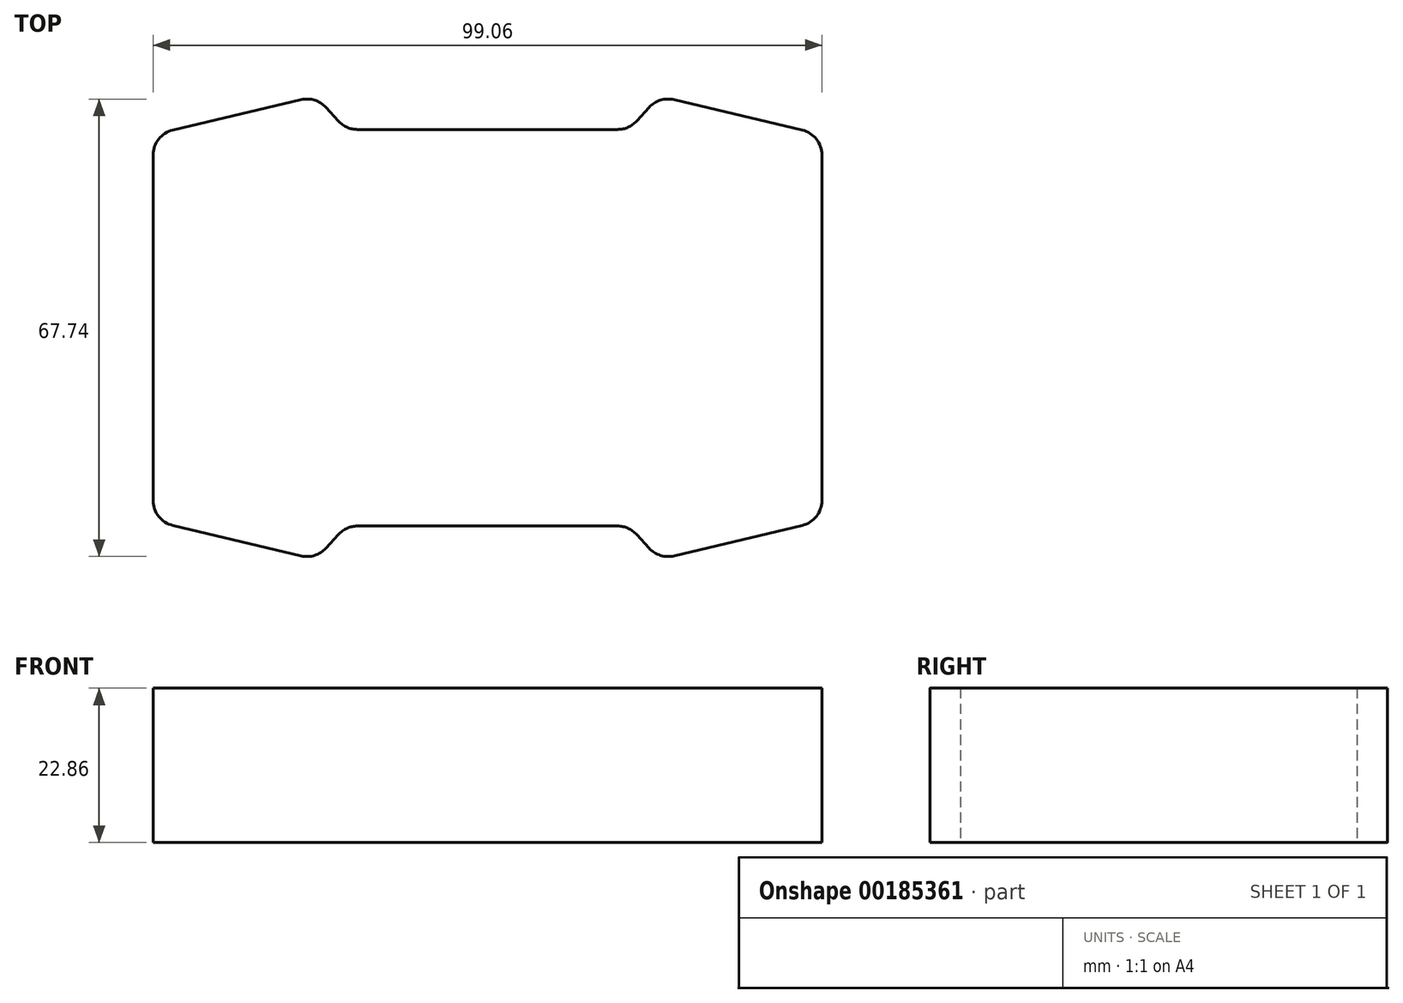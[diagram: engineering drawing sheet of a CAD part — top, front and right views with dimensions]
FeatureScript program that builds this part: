
annotation { "Feature Type Name" : "Feature", "Feature Type Description" : "" }
export const myFeature = defineFeature(function(context is Context, id is Id, definition is map)
    precondition{}
    {
        {
            var Q0;
            Q0=qCreatedBy(makeId("Top.planeOp"),FACE);
            var sketch = newSketch(context, id + "F0", { "sketchPlane" : qUnion([Q0])});
            skLineSegment(sketch, "E0.left", {"start": v(165.1, 95.25) * mm, "end": v(165.1, -95.25) * mm});
            skLineSegment(sketch, "E0.right", {"start": v(-165.1, 95.25) * mm, "end": v(-165.1, -95.25) * mm});
            skPoint(sketch, "E0.middle", {"position": v(0, 0) * mm});
            skLineSegment(sketch, "E1", {"start": v(-165.1, 95.25) * mm, "end": v(-84.78, 114.3) * mm});
            skLineSegment(sketch, "E2", {"start": v(-84.78, 114.3) * mm, "end": v(-69.85, 97.88) * mm});
            skLineSegment(sketch, "E3", {"start": v(-69.85, 97.88) * mm, "end": v(0, 97.88) * mm});
            skLineSegment(sketch, "E4.MirrorCS", {"start": v(165.1, 95.25) * mm, "end": v(84.78, 114.3) * mm});
            skLineSegment(sketch, "E5.MirrorCS", {"start": v(84.78, 114.3) * mm, "end": v(69.85, 97.88) * mm});
            skLineSegment(sketch, "E6.MirrorCS", {"start": v(69.85, 97.88) * mm, "end": v(0, 97.88) * mm});
            skLineSegment(sketch, "E7.MirrorCS", {"start": v(-165.1, -95.25) * mm, "end": v(-84.78, -114.3) * mm});
            skLineSegment(sketch, "E8.MirrorCS", {"start": v(-84.78, -114.3) * mm, "end": v(-69.85, -97.88) * mm});
            skLineSegment(sketch, "E9.MirrorCS", {"start": v(-69.85, -97.88) * mm, "end": v(0, -97.88) * mm});
            skLineSegment(sketch, "E10.MirrorCS", {"start": v(69.85, -97.88) * mm, "end": v(0, -97.88) * mm});
            skLineSegment(sketch, "E11.MirrorCS", {"start": v(84.78, -114.3) * mm, "end": v(69.85, -97.88) * mm});
            skLineSegment(sketch, "E12.MirrorCS", {"start": v(165.1, -95.25) * mm, "end": v(84.78, -114.3) * mm});
            skPoint(sketch, "E13.orphan", {"position": v(-165.1, 114.3) * mm});
            skPoint(sketch, "E14.orphan", {"position": v(165.1, 114.3) * mm});
            skPoint(sketch, "E15.orphan", {"position": v(165.1, -114.3) * mm});
            skPoint(sketch, "E16.orphan", {"position": v(-165.1, -114.3) * mm});
            skSolve(sketch);
        }
        {
            var Q0;
            Q0=qSketchRegion(id+"F0",true);
            extrude(context, id + "F1", {"entities" : qUnion([Q0]), "depth" : 3 * 25.4 * mm});
        }
        {
            var Q0;
            Q0=makeQuery(id+"F1.opExtrude","SWEPT_EDGE",EDGE,{"disambiguationData":[OSD([sQuery(id+"F0.wireOp",EDGE,"E0.right"),sQuery(id+"F0.wireOp",EDGE,"E7.MirrorCS")])]});
            var Q1;
            Q1=makeQuery(id+"F1.opExtrude","SWEPT_EDGE",EDGE,{"disambiguationData":[OSD([sQuery(id+"F0.wireOp",EDGE,"E7.MirrorCS"),sQuery(id+"F0.wireOp",EDGE,"E8.MirrorCS")])]});
            var Q2;
            Q2=makeQuery(id+"F1.opExtrude","SWEPT_EDGE",EDGE,{"disambiguationData":[OSD([sQuery(id+"F0.wireOp",EDGE,"E8.MirrorCS"),sQuery(id+"F0.wireOp",EDGE,"E9.MirrorCS")])]});
            var Q3;
            Q3=makeQuery(id+"F1.opExtrude","SWEPT_EDGE",EDGE,{"disambiguationData":[OSD([sQuery(id+"F0.wireOp",EDGE,"E10.MirrorCS"),sQuery(id+"F0.wireOp",EDGE,"E11.MirrorCS")])]});
            var Q4;
            Q4=makeQuery(id+"F1.opExtrude","SWEPT_EDGE",EDGE,{"disambiguationData":[OSD([sQuery(id+"F0.wireOp",EDGE,"E11.MirrorCS"),sQuery(id+"F0.wireOp",EDGE,"E12.MirrorCS")])]});
            var Q5;
            Q5=makeQuery(id+"F1.opExtrude","SWEPT_EDGE",EDGE,{"disambiguationData":[OSD([sQuery(id+"F0.wireOp",EDGE,"E0.left"),sQuery(id+"F0.wireOp",EDGE,"E12.MirrorCS")])]});
            var Q6;
            Q6=makeQuery(id+"F1.opExtrude","SWEPT_EDGE",EDGE,{"disambiguationData":[OSD([sQuery(id+"F0.wireOp",EDGE,"E0.left"),sQuery(id+"F0.wireOp",EDGE,"E4.MirrorCS")])]});
            var Q7;
            Q7=makeQuery(id+"F1.opExtrude","SWEPT_EDGE",EDGE,{"disambiguationData":[OSD([sQuery(id+"F0.wireOp",EDGE,"E4.MirrorCS"),sQuery(id+"F0.wireOp",EDGE,"E5.MirrorCS")])]});
            var Q8;
            Q8=makeQuery(id+"F1.opExtrude","SWEPT_EDGE",EDGE,{"disambiguationData":[OSD([sQuery(id+"F0.wireOp",EDGE,"E5.MirrorCS"),sQuery(id+"F0.wireOp",EDGE,"E6.MirrorCS")])]});
            var Q9;
            Q9=makeQuery(id+"F1.opExtrude","SWEPT_EDGE",EDGE,{"disambiguationData":[OSD([sQuery(id+"F0.wireOp",EDGE,"E2"),sQuery(id+"F0.wireOp",EDGE,"E3")])]});
            var Q10;
            Q10=makeQuery(id+"F1.opExtrude","SWEPT_EDGE",EDGE,{"disambiguationData":[OSD([sQuery(id+"F0.wireOp",EDGE,"E1"),sQuery(id+"F0.wireOp",EDGE,"E2")])]});
            var Q11;
            Q11=makeQuery(id+"F1.opExtrude","SWEPT_EDGE",EDGE,{"disambiguationData":[OSD([sQuery(id+"F0.wireOp",EDGE,"E0.right"),sQuery(id+"F0.wireOp",EDGE,"E1")])]});
            fillet(context, id + "F2", {"entities" : qUnion([Q0, Q1, Q2, Q3, Q4, Q5, Q6, Q7, Q8, Q9, Q10, Q11]), "radius" : 12.7 * mm, "tangentPropagation" : true, "allowEdgeOverflow" : false});
        }
        {
            var Q0;
            Q0=makeQuery(id+"F1.opExtrude","SWEPT_BODY",BODY,{"disambiguationData":[OSD([sQuery(id+"F0.wireOp",EDGE,"E0.left"),sQuery(id+"F0.wireOp",EDGE,"E0.right"),sQuery(id+"F0.wireOp",EDGE,"E1"),sQuery(id+"F0.wireOp",EDGE,"E2"),sQuery(id+"F0.wireOp",EDGE,"E3"),sQuery(id+"F0.wireOp",EDGE,"E4.MirrorCS"),sQuery(id+"F0.wireOp",EDGE,"E5.MirrorCS"),sQuery(id+"F0.wireOp",EDGE,"E6.MirrorCS"),sQuery(id+"F0.wireOp",EDGE,"E7.MirrorCS"),sQuery(id+"F0.wireOp",EDGE,"E8.MirrorCS"),sQuery(id+"F0.wireOp",EDGE,"E9.MirrorCS"),sQuery(id+"F0.wireOp",EDGE,"E10.MirrorCS"),sQuery(id+"F0.wireOp",EDGE,"E11.MirrorCS"),sQuery(id+"F0.wireOp",EDGE,"E12.MirrorCS")])]});
            var Q1;
            Q1=qCreatedBy(makeId("Origin.pointOp"),VERTEX);
            transform(context, id + "F3", {"entities" : qUnion([Q0]), "transformType" : TransformType.SCALE_UNIFORMLY, "scale" : .3, "scalePoint" : qUnion([Q1]), "makeCopy" : false});
        }
    });
